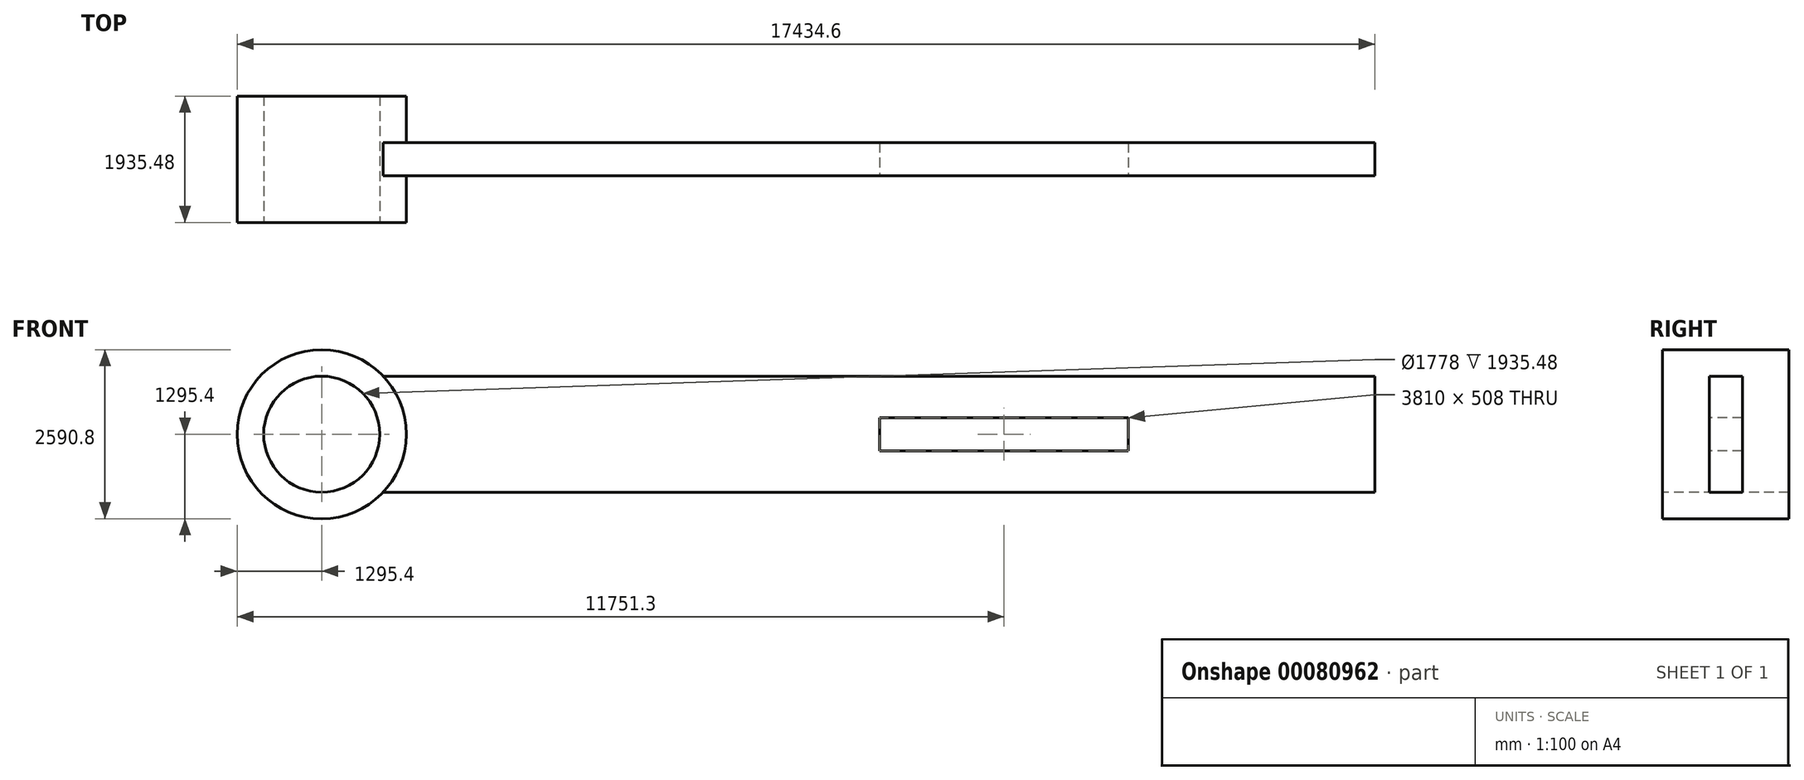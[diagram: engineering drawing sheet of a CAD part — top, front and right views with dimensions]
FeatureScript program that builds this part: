
annotation { "Feature Type Name" : "Feature", "Feature Type Description" : "" }
export const myFeature = defineFeature(function(context is Context, id is Id, definition is map)
    precondition{}
    {
        {
            var Q0;
            Q0=qCreatedBy(makeId("Right.planeOp"),FACE);
            var sketch = newSketch(context, id + "F0", { "sketchPlane" : qUnion([Q0])});
            skLineSegment(sketch, "E0.bottom", {"start": v(0, 1295.4) * mm, "end": v(1935.48, 1295.4) * mm});
            skLineSegment(sketch, "E0.top", {"start": v(0, 889) * mm, "end": v(1935.48, 889) * mm});
            skLineSegment(sketch, "E0.left", {"start": v(0, 1295.4) * mm, "end": v(0, 889) * mm});
            skLineSegment(sketch, "E0.right", {"start": v(1935.48, 1295.4) * mm, "end": v(1935.48, 889) * mm});
            skLineSegment(sketch, "E1", {"start": v(0, 0) * mm, "end": v(733.65, 0) * mm});
            skSolve(sketch);
        }
        {
            var Q0;
            Q0=makeQuery(id+"F0.imprint","IMPRINT",FACE,{"disambiguationData":[TD([[makeQuery(id+"F0.imprint","IMPRINT",EDGE,{"derivedFrom":sQuery(id+"F0.wireOp",EDGE,"E0.bottom")}),-1.0]])]});
            var Q1;
            Q1=sQuery(id+"F0.wireOp",EDGE,"E1");
            revolve(context, id + "F1", {"entities" : qUnion([Q0]), "axis" : qUnion([Q1]), "revolveType" : RevolveType.FULL});
        }
        {
            var Q0;
            Q0=qCreatedBy(makeId("Right.planeOp"),FACE);
            cPlane(context, id + "F2", {"entities" : qUnion([Q0]), "cplaneType" : CPlaneType.OFFSET, "offset" : 899.16 * mm, "width" : 152.4 * mm, "height" : 152.4 * mm});
        }
        {
            var Q0;
            Q0=qCreatedBy(id+"F2.planeOp",FACE);
            var sketch = newSketch(context, id + "F3", { "sketchPlane" : qUnion([Q0])});
            skLineSegment(sketch, "E2.bottom", {"start": v(1221.74, -889) * mm, "end": v(713.74, -889) * mm});
            skLineSegment(sketch, "E2.top", {"start": v(1221.74, 889) * mm, "end": v(713.74, 889) * mm});
            skLineSegment(sketch, "E2.left", {"start": v(1221.74, -889) * mm, "end": v(1221.74, 889) * mm});
            skLineSegment(sketch, "E2.right", {"start": v(713.74, -889) * mm, "end": v(713.74, 889) * mm});
            skPoint(sketch, "E2.middle", {"position": v(967.74, 0) * mm});
            skSolve(sketch);
        }
        {
            var Q0;
            Q0 = qSketchRegion(id + "F3", true);
            extrude(context, id + "F4", {"entities" : qUnion([Q0]), "operationType" : NewBodyOperationType.ADD, "depth" : 15240 * mm});
        }
        {
            var Q0;
            Q0=makeQuery(id+"F4.opExtrude","SWEPT_FACE",FACE,{"disambiguationData":[OSD([sQuery(id+"F3.wireOp",EDGE,"E2.right")])]});
            var sketch = newSketch(context, id + "F5", { "sketchPlane" : qUnion([Q0])});
            skLineSegment(sketch, "E3.bottom", {"start": v(8550.94, 254) * mm, "end": v(12360.94, 254) * mm});
            skLineSegment(sketch, "E3.top", {"start": v(8550.94, -254) * mm, "end": v(12360.94, -254) * mm});
            skLineSegment(sketch, "E3.left", {"start": v(8550.94, 254) * mm, "end": v(8550.94, -254) * mm});
            skLineSegment(sketch, "E3.right", {"start": v(12360.94, 254) * mm, "end": v(12360.94, -254) * mm});
            skPoint(sketch, "E3.middle", {"position": v(10455.94, 0) * mm});
            skSolve(sketch);
        }
        {
            var Q0;
            Q0 = qSketchRegion(id + "F5", true);
            extrude(context, id + "F6", {"entities" : qUnion([Q0]), "operationType" : NewBodyOperationType.REMOVE, "endBound" : BoundingType.THROUGH_ALL, "oppositeDirection" : true, "depth" : 25.4 * mm});
        }
    });
